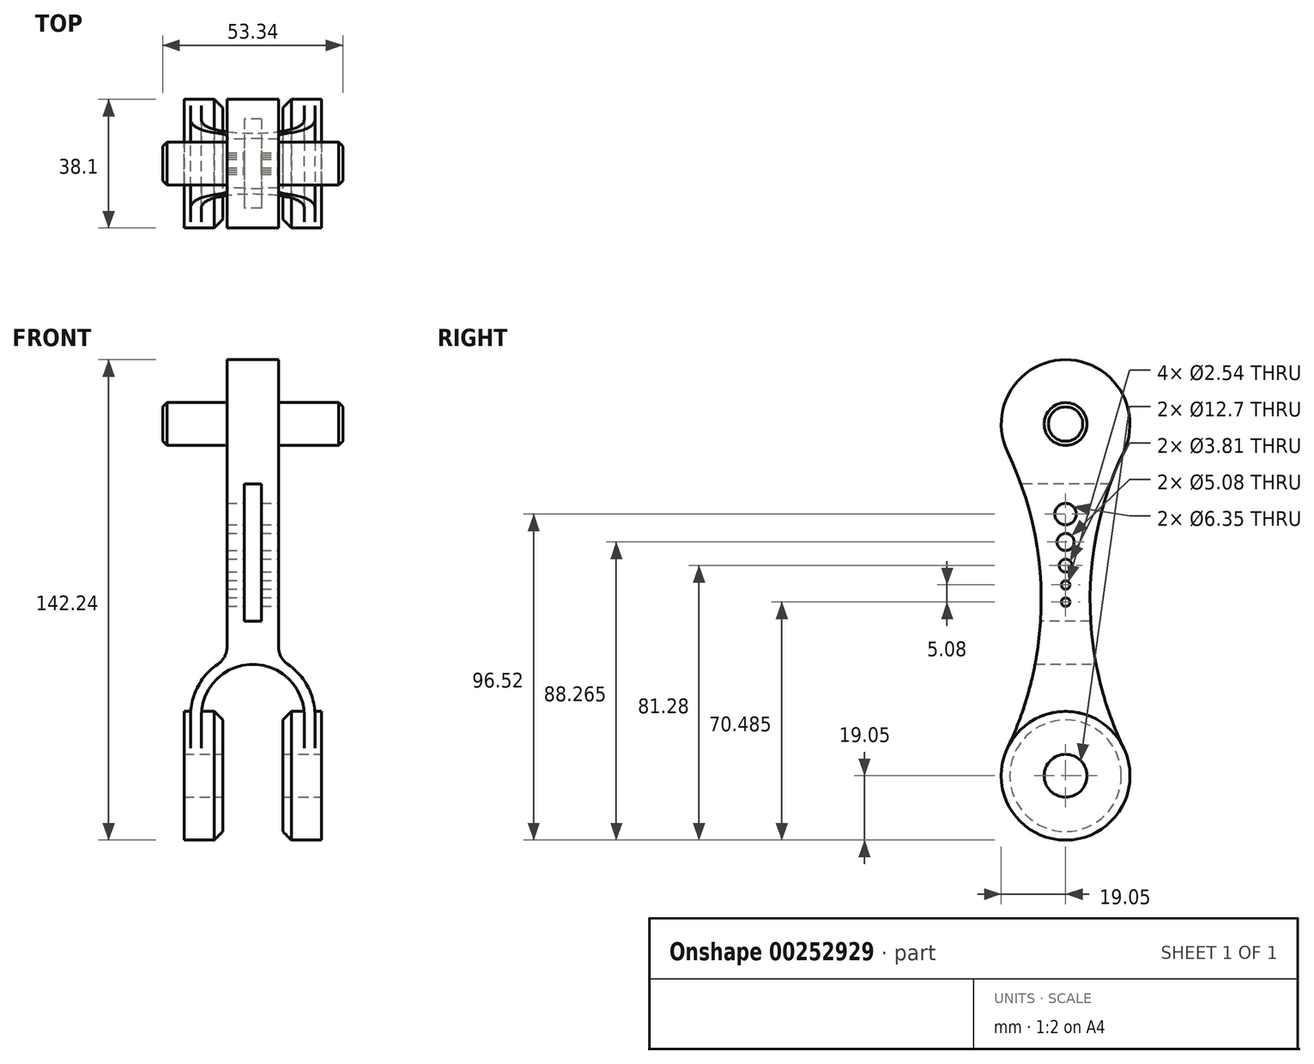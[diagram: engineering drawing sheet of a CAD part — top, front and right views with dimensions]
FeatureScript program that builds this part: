
annotation { "Feature Type Name" : "Feature", "Feature Type Description" : "" }
export const myFeature = defineFeature(function(context is Context, id is Id, definition is map)
    precondition{}
    {
        {
            var Q0;
            Q0=qCreatedBy(makeId("Front.planeOp"),FACE);
            var sketch = newSketch(context, id + "F0", { "sketchPlane" : qUnion([Q0])});
            skPoint(sketch, "E0.middle", {"position": v(0, -15.24) * mm});
            skPoint(sketch, "E1.visualSharp", {"position": v(20.32, -12.7) * mm});
            skLineSegment(sketch, "E2.bottom", {"start": v(-7.62, 0) * mm, "end": v(7.62, 0) * mm});
            skLineSegment(sketch, "E2.left", {"start": v(-7.62, 0) * mm, "end": v(-7.62, -24.51) * mm});
            skLineSegment(sketch, "E2.right", {"start": v(7.62, 0) * mm, "end": v(7.62, -24.51) * mm});
            skArc(sketch, "E3", {"start": v(15.24, -48.26) * mm, "mid": v(0, -33.02) * mm, "end": v(-15.24, -48.26) * mm});
            skArc(sketch, "E4", {"start": v(18.41, -48.26) * mm, "mid": v(16.29, -39.66) * mm, "end": v(10.39, -33.05) * mm});
            skLineSegment(sketch, "E5.top", {"start": v(16.76, -66.58) * mm, "end": v(16.9, -66.58) * mm});
            skLineSegment(sketch, "E5.left", {"start": v(15.24, -48.26) * mm, "end": v(15.24, -65.05) * mm});
            skLineSegment(sketch, "E5.right", {"start": v(18.41, -48.26) * mm, "end": v(18.41, -65.05) * mm});
            skLineSegment(sketch, "E6.top", {"start": v(-16.76, -66.04) * mm, "end": v(-16.9, -66.04) * mm});
            skLineSegment(sketch, "E6.left", {"start": v(-15.24, -48.26) * mm, "end": v(-15.24, -64.52) * mm});
            skLineSegment(sketch, "E6.right", {"start": v(-18.41, -48.26) * mm, "end": v(-18.41, -64.52) * mm});
            skLineSegment(sketch, "E7", {"start": v(7.62, -24.51) * mm, "end": v(7.62, -27.81) * mm});
            skLineSegment(sketch, "E8", {"start": v(-7.62, -24.51) * mm, "end": v(-7.62, -27.81) * mm});
            skPoint(sketch, "E9.visualSharp", {"position": v(15.24, -66.58) * mm});
            skArc(sketch, "E9.filletArc", {"start": v(15.24, -65.05) * mm, "mid": v(15.69, -66.13) * mm, "end": v(16.76, -66.58) * mm});
            skPoint(sketch, "E10.visualSharp", {"position": v(18.41, -66.58) * mm});
            skArc(sketch, "E10.filletArc", {"start": v(16.9, -66.58) * mm, "mid": v(17.97, -66.13) * mm, "end": v(18.41, -65.05) * mm});
            skPoint(sketch, "E11.visualSharp", {"position": v(-18.41, -66.04) * mm});
            skArc(sketch, "E11.filletArc", {"start": v(-18.41, -64.52) * mm, "mid": v(-17.97, -65.6) * mm, "end": v(-16.9, -66.04) * mm});
            skPoint(sketch, "E12.visualSharp", {"position": v(-15.24, -66.04) * mm});
            skArc(sketch, "E12.filletArc", {"start": v(-16.76, -66.04) * mm, "mid": v(-15.69, -65.6) * mm, "end": v(-15.24, -64.52) * mm});
            skArc(sketch, "E13.trimOffspring", {"start": v(-10.39, -33.05) * mm, "mid": v(-16.29, -39.66) * mm, "end": v(-18.41, -48.26) * mm});
            skPoint(sketch, "E14.visualSharp", {"position": v(7.62, -31.5) * mm});
            skArc(sketch, "E14.filletArc", {"start": v(7.62, -27.81) * mm, "mid": v(8.35, -30.78) * mm, "end": v(10.39, -33.05) * mm});
            skPoint(sketch, "E15.visualSharp", {"position": v(-7.62, -31.5) * mm});
            skArc(sketch, "E15.filletArc", {"start": v(-10.39, -33.05) * mm, "mid": v(-8.35, -30.78) * mm, "end": v(-7.62, -27.81) * mm});
            skSolve(sketch);
        }
        {
            var Q0;
            Q0=qSketchRegion(id+"F0",true);
            extrude(context, id + "F1", {"entities" : qUnion([Q0]), "endBound" : BoundingType.SYMMETRIC, "depth" : 44.45 * mm});
        }
        {
            var Q0;
            Q0=qCreatedBy(makeId("Right.planeOp"),FACE);
            var sketch = newSketch(context, id + "F2", { "sketchPlane" : qUnion([Q0])});
            skCircle(sketch, "E16", {"center": v(0, -66.04) * mm, "radius": 6.35 * mm});
            skSolve(sketch);
        }
        {
            var Q0;
            Q0=qCreatedBy(makeId("Right.planeOp"),FACE);
            var sketch = newSketch(context, id + "F3", { "sketchPlane" : qUnion([Q0])});
            skCircle(sketch, "E17", {"center": v(0, -66.04) * mm, "radius": 19.05 * mm});
            skSolve(sketch);
        }
        {
            var Q0;
            Q0=qSketchRegion(id+"F3",true);
            extrude(context, id + "F4", {"entities" : qUnion([Q0]), "operationType" : NewBodyOperationType.ADD, "endBound" : BoundingType.SYMMETRIC, "depth" : 40.64 * mm});
        }
        {
            var Q0;
            Q0=qCreatedBy(makeId("Front.planeOp"),FACE);
            var sketch = newSketch(context, id + "F5", { "sketchPlane" : qUnion([Q0])});
            skLineSegment(sketch, "E18.bottom", {"start": v(8.9, -85.1) * mm, "end": v(-8.89, -85.1) * mm});
            skLineSegment(sketch, "E18.top", {"start": v(8.9, -47) * mm, "end": v(-8.89, -47) * mm});
            skLineSegment(sketch, "E18.left", {"start": v(8.9, -85.1) * mm, "end": v(8.9, -47) * mm});
            skLineSegment(sketch, "E18.right", {"start": v(-8.89, -85.1) * mm, "end": v(-8.89, -47) * mm});
            skPoint(sketch, "E18.middle", {"position": v(0, -66.04) * mm});
            skSolve(sketch);
        }
        {
            var Q0;
            Q0=qSketchRegion(id+"F2",true);
            extrude(context, id + "F6", {"entities" : qUnion([Q0]), "operationType" : NewBodyOperationType.REMOVE, "endBound" : BoundingType.SYMMETRIC, "oppositeDirection" : true, "depth" : 76.2 * mm});
        }
        {
            var Q0;
            Q0=qSketchRegion(id+"F5",true);
            extrude(context, id + "F7", {"entities" : qUnion([Q0]), "operationType" : NewBodyOperationType.REMOVE, "endBound" : BoundingType.SYMMETRIC, "oppositeDirection" : true, "depth" : 38.1 * mm});
        }
        {
            var Q0;
            Q0=makeQuery(id+"F7.boolean.opBoolean","INTERSECT",EDGE,{"derivedFrom":[makeQuery(id+"F4.opExtrude","SWEPT_FACE",FACE,{"disambiguationData":[OSD([sQuery(id+"F3.wireOp",EDGE,"E17")])]}),makeQuery(id+"F7.opExtrude","SWEPT_FACE",FACE,{"disambiguationData":[OSD([sQuery(id+"F5.wireOp",EDGE,"E18.right")])]})]});
            var Q1;
            Q1=makeQuery(id+"F7.boolean.opBoolean","INTERSECT",EDGE,{"derivedFrom":[makeQuery(id+"F4.opExtrude","SWEPT_FACE",FACE,{"disambiguationData":[OSD([sQuery(id+"F3.wireOp",EDGE,"E17")])]}),makeQuery(id+"F7.opExtrude","SWEPT_FACE",FACE,{"disambiguationData":[OSD([sQuery(id+"F5.wireOp",EDGE,"E18.left")])]})]});
            chamfer(context, id + "F8", {"entities" : qUnion([Q0, Q1]), "width" : 2.54 * mm, "tangentPropagation" : true});
        }
        {
            var Q0;
            Q0=qCreatedBy(makeId("Right.planeOp"),FACE);
            var sketch = newSketch(context, id + "F9", { "sketchPlane" : qUnion([Q0])});
            skArc(sketch, "E19", {"start": v(19.05, 38.09) * mm, "mid": v(0, 57.15) * mm, "end": v(-19.05, 38.09) * mm});
            skLineSegment(sketch, "E20.top", {"start": v(-19.05, -0.01) * mm, "end": v(19.05, -0.01) * mm});
            skLineSegment(sketch, "E20.left", {"start": v(-19.05, 38.09) * mm, "end": v(-19.05, -0.01) * mm});
            skLineSegment(sketch, "E20.right", {"start": v(19.05, 38.09) * mm, "end": v(19.05, -0.01) * mm});
            skSolve(sketch);
        }
        {
            var Q0;
            Q0=qSketchRegion(id+"F9",true);
            extrude(context, id + "F10", {"entities" : qUnion([Q0]), "operationType" : NewBodyOperationType.ADD, "endBound" : BoundingType.SYMMETRIC, "depth" : 15.24 * mm});
        }
        {
            var Q0;
            Q0=qCreatedBy(makeId("Right.planeOp"),FACE);
            var sketch = newSketch(context, id + "F11", { "sketchPlane" : qUnion([Q0])});
            skCircle(sketch, "E21", {"center": v(0, 38.1) * mm, "radius": 6.35 * mm});
            skSolve(sketch);
        }
        {
            var Q0;
            Q0=qSketchRegion(id+"F11",true);
            extrude(context, id + "F12", {"entities" : qUnion([Q0]), "operationType" : NewBodyOperationType.ADD, "depth" : 26.67 * mm});
        }
        {
            var Q0;
            Q0=makeQuery(id+"F12.opExtrude","CAP_EDGE",EDGE,{"disambiguationData":[OSD([sQuery(id+"F11.wireOp",EDGE,"E21")])],"isStart":true});
            var Q1;
            Q1=makeQuery(id+"F12.opExtrude","CAP_EDGE",EDGE,{"disambiguationData":[OSD([sQuery(id+"F11.wireOp",EDGE,"E21")])],"isStart":false});
            chamfer(context, id + "F13", {"entities" : qUnion([Q0, Q1]), "width" : 1.27 * mm, "tangentPropagation" : true});
        }
        {
            var Q0;
            Q0=qCreatedBy(makeId("Right.planeOp"),FACE);
            var sketch = newSketch(context, id + "F14", { "sketchPlane" : qUnion([Q0])});
            skArc(sketch, "E22", {"start": v(17.18, 29.88) * mm, "mid": v(0, 57.15) * mm, "end": v(-17.18, 29.88) * mm});
            skArc(sketch, "E23", {"start": v(-17.18, -57.82) * mm, "mid": v(0, -85.1) * mm, "end": v(17.18, -57.82) * mm});
            skArc(sketch, "E24", {"start": v(17.18, 29.88) * mm, "mid": v(7.24, -13.97) * mm, "end": v(17.18, -57.82) * mm});
            skPoint(sketch, "E25.center.orphan", {"position": v(45.72, -6.35) * mm});
            skPoint(sketch, "E26.center.orphan", {"position": v(-45.72, -6.35) * mm});
            skArc(sketch, "E27", {"start": v(-17.18, -57.82) * mm, "mid": v(-7.24, -13.97) * mm, "end": v(-17.18, 29.88) * mm});
            skSolve(sketch);
        }
        {
            var Q0;
            Q0=qSketchRegion(id+"F14",true);
            extrude(context, id + "F15", {"entities" : qUnion([Q0]), "operationType" : NewBodyOperationType.INTERSECT, "endBound" : BoundingType.SYMMETRIC, "depth" : 76.2 * mm});
        }
        {
            var Q0;
            Q0=qCreatedBy(makeId("Front.planeOp"),FACE);
            var sketch = newSketch(context, id + "F16", { "sketchPlane" : qUnion([Q0])});
            skLineSegment(sketch, "E28.bottom", {"start": v(-2.54, -20.32) * mm, "end": v(2.54, -20.32) * mm});
            skLineSegment(sketch, "E28.top", {"start": v(-2.54, 20.32) * mm, "end": v(2.54, 20.32) * mm});
            skLineSegment(sketch, "E28.left", {"start": v(-2.54, -20.32) * mm, "end": v(-2.54, 20.32) * mm});
            skLineSegment(sketch, "E28.right", {"start": v(2.54, -20.32) * mm, "end": v(2.54, 20.32) * mm});
            skSolve(sketch);
        }
        {
            var Q0;
            Q0=qSketchRegion(id+"F16",true);
            extrude(context, id + "F17", {"entities" : qUnion([Q0]), "operationType" : NewBodyOperationType.REMOVE, "endBound" : BoundingType.SYMMETRIC, "oppositeDirection" : true, "depth" : 50.8 * mm});
        }
        {
            var Q0;
            Q0=makeQuery(id+"F10.boolean.opBoolean","MERGE",FACE,{"derivedFrom":[makeQuery(id+"F1.opExtrude","SWEPT_FACE",FACE,{"disambiguationData":[OSD([sQuery(id+"F0.wireOp",EDGE,"E2.left")])]}),makeQuery(id+"F10.opExtrude","CAP_FACE",FACE,{"disambiguationData":[OSD([sQuery(id+"F9.wireOp",EDGE,"E19"),sQuery(id+"F9.wireOp",EDGE,"E20.top"),sQuery(id+"F9.wireOp",EDGE,"E20.left"),sQuery(id+"F9.wireOp",EDGE,"E20.right")])],"isStart":true})]});
            var sketch = newSketch(context, id + "F18", { "sketchPlane" : qUnion([Q0])});
            skCircle(sketch, "E29", {"center": v(0, 38.1) * mm, "radius": 6.35 * mm});
            skSolve(sketch);
        }
        {
            var Q0;
            Q0=qSketchRegion(id+"F18",true);
            extrude(context, id + "F19", {"entities" : qUnion([Q0]), "operationType" : NewBodyOperationType.ADD, "depth" : 19.05 * mm});
        }
        {
            var Q0;
            Q0=qCreatedBy(makeId("Right.planeOp"),FACE);
            var sketch = newSketch(context, id + "F20", { "sketchPlane" : qUnion([Q0])});
            skCircle(sketch, "E30", {"center": v(0, -3.8) * mm, "radius": 1.9 * mm});
            skCircle(sketch, "E31", {"center": v(0, -9.52) * mm, "radius": 1.27 * mm});
            skCircle(sketch, "E32", {"center": v(0, -14.6) * mm, "radius": 1.27 * mm});
            skCircle(sketch, "E33", {"center": v(0, 3.18) * mm, "radius": 2.54 * mm});
            skCircle(sketch, "E34", {"center": v(0, 11.43) * mm, "radius": 3.18 * mm});
            skSolve(sketch);
        }
        {
            var Q0;
            Q0=qSketchRegion(id+"F20",true);
            extrude(context, id + "F21", {"entities" : qUnion([Q0]), "operationType" : NewBodyOperationType.REMOVE, "endBound" : BoundingType.SYMMETRIC, "oppositeDirection" : true, "depth" : 25.4 * mm});
        }
        {
            var Q0;
            Q0=makeQuery(id+"F19.opExtrude","CAP_EDGE",EDGE,{"disambiguationData":[OSD([sQuery(id+"F18.wireOp",EDGE,"E29")])],"isStart":false});
            chamfer(context, id + "F22", {"entities" : qUnion([Q0]), "width" : 1.27 * mm, "tangentPropagation" : true});
        }
        {
            var Q0;
            Q0=qCreatedBy(makeId("Front.planeOp"),FACE);
            var sketch = newSketch(context, id + "F23", { "sketchPlane" : qUnion([Q0])});
            skPoint(sketch, "E35", {"position": v(0, 38.1) * mm});
            skLineSegment(sketch, "E36", {"start": v(0, 0) * mm, "end": v(0, 38.1) * mm, "construction": true});
            skSolve(sketch);
        }
        {
            var Q0;
            Q0=makeQuery(id+"F1.opExtrude","SWEPT_BODY",BODY,{"disambiguationData":[OSD([sQuery(id+"F0.wireOp",EDGE,"E2.bottom"),sQuery(id+"F0.wireOp",EDGE,"E2.left"),sQuery(id+"F0.wireOp",EDGE,"E2.right"),sQuery(id+"F0.wireOp",EDGE,"E3"),sQuery(id+"F0.wireOp",EDGE,"E4"),sQuery(id+"F0.wireOp",EDGE,"E5.top"),sQuery(id+"F0.wireOp",EDGE,"E5.left"),sQuery(id+"F0.wireOp",EDGE,"E5.right"),sQuery(id+"F0.wireOp",EDGE,"E6.top"),sQuery(id+"F0.wireOp",EDGE,"E6.left"),sQuery(id+"F0.wireOp",EDGE,"E6.right"),sQuery(id+"F0.wireOp",EDGE,"E7"),sQuery(id+"F0.wireOp",EDGE,"E8"),sQuery(id+"F0.wireOp",EDGE,"E9.filletArc"),sQuery(id+"F0.wireOp",EDGE,"E10.filletArc"),sQuery(id+"F0.wireOp",EDGE,"E11.filletArc"),sQuery(id+"F0.wireOp",EDGE,"E12.filletArc"),sQuery(id+"F0.wireOp",EDGE,"E13.trimOffspring"),sQuery(id+"F0.wireOp",EDGE,"E14.filletArc"),sQuery(id+"F0.wireOp",EDGE,"E15.filletArc")])]});
            var Q1;
            Q1=sQuery(id+"F23.wireOp",EDGE,"E36");
            transform(context, id + "F24", {"entities" : qUnion([Q0]), "transformType" : TransformType.TRANSLATION_ENTITY, "oppositeDirectionEntity" : true, "transformLine" : qUnion([Q1]), "makeCopy" : false});
        }
    });
